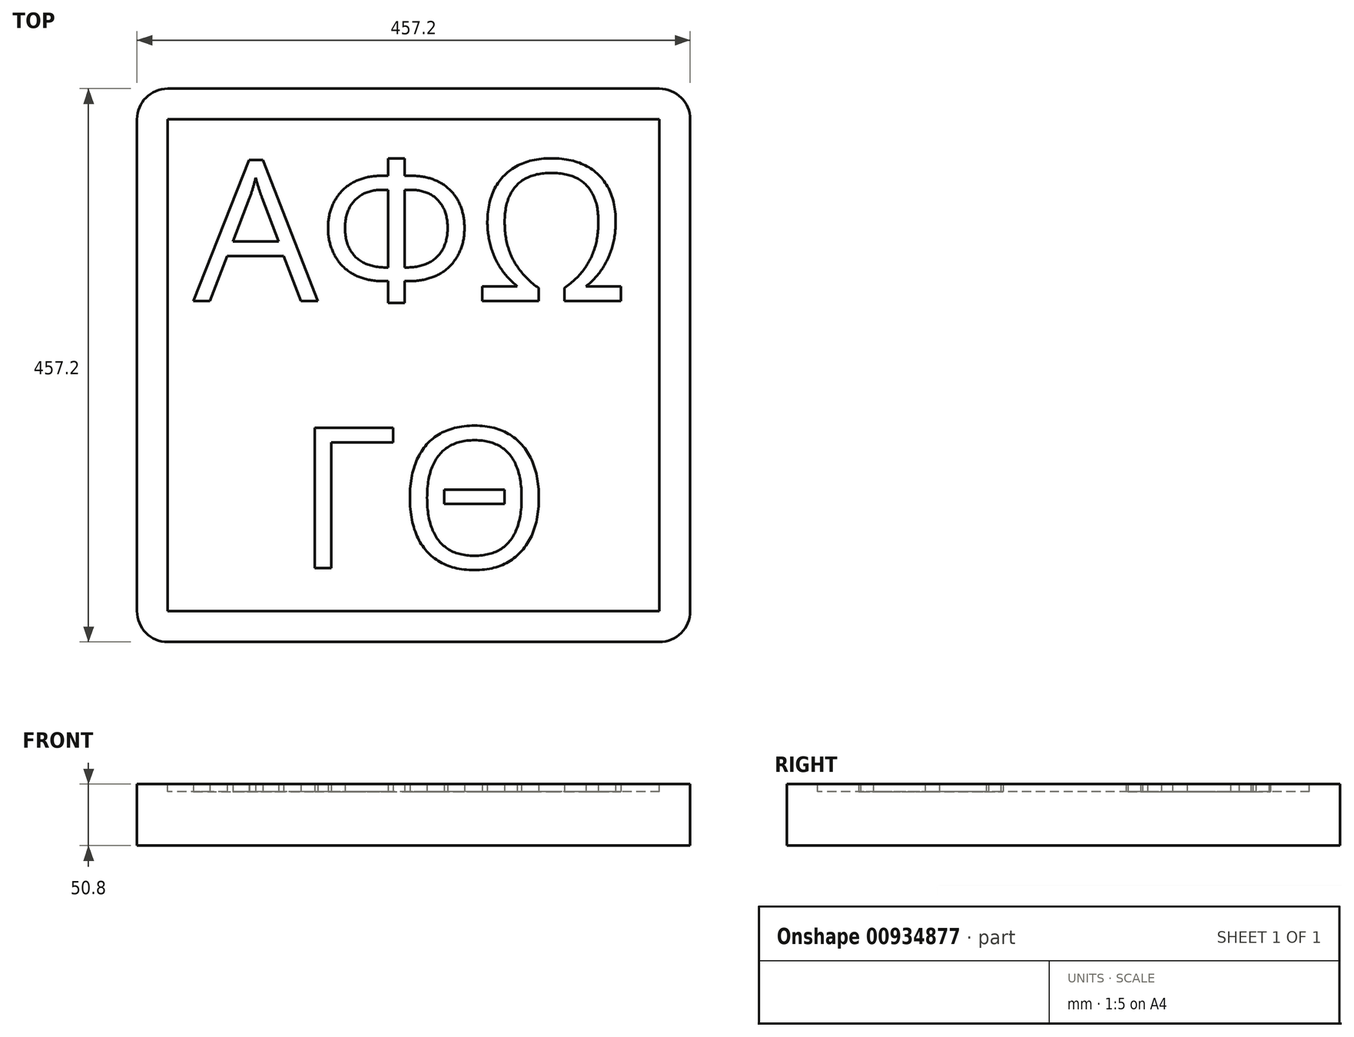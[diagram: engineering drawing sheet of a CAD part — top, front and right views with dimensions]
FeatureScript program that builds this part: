
annotation { "Feature Type Name" : "Feature", "Feature Type Description" : "" }
export const myFeature = defineFeature(function(context is Context, id is Id, definition is map)
    precondition{}
    {
        {
            var Q0;
            Q0=qCreatedBy(makeId("Top.planeOp"),FACE);
            var sketch = newSketch(context, id + "F0", { "sketchPlane" : qUnion([Q0])});
            skLineSegment(sketch, "E0.bottom", {"start": v(228.6, 228.6) * mm, "end": v(-228.6, 228.6) * mm});
            skLineSegment(sketch, "E0.top", {"start": v(228.6, -228.6) * mm, "end": v(-228.6, -228.6) * mm});
            skLineSegment(sketch, "E0.left", {"start": v(228.6, 228.6) * mm, "end": v(228.6, -228.6) * mm});
            skLineSegment(sketch, "E0.right", {"start": v(-228.6, 228.6) * mm, "end": v(-228.6, -228.6) * mm});
            skPoint(sketch, "E0.middle", {"position": v(0, 0) * mm});
            skSolve(sketch);
        }
        {
            var Q0;
            Q0=makeQuery(id+"F0.imprint","IMPRINT",FACE,{"disambiguationData":[TD([[makeQuery(id+"F0.imprint","IMPRINT",EDGE,{"derivedFrom":sQuery(id+"F0.wireOp",EDGE,"E0.bottom")}),1.0]])]});
            extrude(context, id + "F1", {"entities" : qUnion([Q0]), "depth" : 50.8 * mm, "offsetDistance" : 25.4 * mm});
        }
        {
            var Q0;
            Q0=makeQuery(id+"F1.opExtrude","SWEPT_EDGE",EDGE,{"disambiguationData":[OSD([sQuery(id+"F0.wireOp",EDGE,"E0.top"),sQuery(id+"F0.wireOp",EDGE,"E0.right")])]});
            var Q1;
            Q1=makeQuery(id+"F1.opExtrude","SWEPT_EDGE",EDGE,{"disambiguationData":[OSD([sQuery(id+"F0.wireOp",EDGE,"E0.top"),sQuery(id+"F0.wireOp",EDGE,"E0.left")])]});
            var Q2;
            Q2=makeQuery(id+"F1.opExtrude","SWEPT_EDGE",EDGE,{"disambiguationData":[OSD([sQuery(id+"F0.wireOp",EDGE,"E0.bottom"),sQuery(id+"F0.wireOp",EDGE,"E0.left")])]});
            var Q3;
            Q3=makeQuery(id+"F1.opExtrude","SWEPT_EDGE",EDGE,{"disambiguationData":[OSD([sQuery(id+"F0.wireOp",EDGE,"E0.bottom"),sQuery(id+"F0.wireOp",EDGE,"E0.right")])]});
            fillet(context, id + "F2", {"entities" : qUnion([Q0, Q1, Q2, Q3]), "radius" : 25.4 * mm, "tangentPropagation" : true, "allowEdgeOverflow" : false});
        }
        {
            var Q0;
            Q0=makeQuery(id+"F1.opExtrude","CAP_FACE",FACE,{"disambiguationData":[OSD([sQuery(id+"F0.wireOp",EDGE,"E0.bottom"),sQuery(id+"F0.wireOp",EDGE,"E0.top"),sQuery(id+"F0.wireOp",EDGE,"E0.left"),sQuery(id+"F0.wireOp",EDGE,"E0.right")])],"isStart":false});
            var sketch = newSketch(context, id + "F3", { "sketchPlane" : qUnion([Q0])});
            skLineSegment(sketch, "E1.bottom", {"start": v(203.2, 203.2) * mm, "end": v(-203.2, 203.2) * mm});
            skLineSegment(sketch, "E1.top", {"start": v(203.2, -203.2) * mm, "end": v(-203.2, -203.2) * mm});
            skLineSegment(sketch, "E1.left", {"start": v(203.2, 203.2) * mm, "end": v(203.2, -203.2) * mm});
            skLineSegment(sketch, "E1.right", {"start": v(-203.2, 203.2) * mm, "end": v(-203.2, -203.2) * mm});
            skPoint(sketch, "E1.middle", {"position": v(0, 0) * mm});
            skSolve(sketch);
        }
        {
            var Q0;
            Q0=makeQuery(id+"F3.imprint","IMPRINT",FACE,{"disambiguationData":[TD([[makeQuery(id+"F3.imprint","IMPRINT",EDGE,{"derivedFrom":sQuery(id+"F3.wireOp",EDGE,"E1.bottom")}),1.0]])]});
            extrude(context, id + "F4", {"entities" : qUnion([Q0]), "operationType" : NewBodyOperationType.REMOVE, "oppositeDirection" : true, "depth" : 6.35 * mm, "offsetDistance" : 25.4 * mm});
        }
        {
            var Q0;
            Q0=makeQuery(id+"F4.boolean.opBoolean","COPY",FACE,{"derivedFrom":makeQuery(id+"F4.opExtrude","CAP_FACE",FACE,{"disambiguationData":[OSD([sQuery(id+"F3.wireOp",EDGE,"E1.bottom"),sQuery(id+"F3.wireOp",EDGE,"E1.top"),sQuery(id+"F3.wireOp",EDGE,"E1.left"),sQuery(id+"F3.wireOp",EDGE,"E1.right")])],"isStart":false})});
            var sketch = newSketch(context, id + "F5", { "sketchPlane" : qUnion([Q0])});
            skText(sketch, "E2", { "text": "ΑΦΩ\n  ΓΘ", "fontName": "OpenSans-Regular.ttf"});
            skLineSegment(sketch, "E3", {"start": v(-82.05, -170.18) * mm, "end": v(203.2, -170.18) * mm});
            const initialGuessF5  = {"E2": [-0.18186, 0.05325, 1, 0, 0.11693]};
            skSetInitialGuess(sketch, initialGuessF5);
            skSolve(sketch);
        }
        {
            var Q0;
            Q0=makeQuery(id+"F5.imprint","IMPRINT",FACE,{"disambiguationData":[TD([[makeQuery(id+"F5.imprint","IMPRINT",EDGE,{"derivedFrom":sQuery(id+"F5.wireOp",EDGE,"E2.sketch_text.stroke-73")}),-1.0]])]});
            var Q1;
            Q1=makeQuery(id+"F5.imprint","IMPRINT",FACE,{"disambiguationData":[TD([[makeQuery(id+"F5.imprint","IMPRINT",EDGE,{"derivedFrom":sQuery(id+"F5.wireOp",EDGE,"E2.sketch_text.stroke-79")}),-1.0]])]});
            var Q2;
            Q2=makeQuery(id+"F5.imprint","IMPRINT",FACE,{"disambiguationData":[TD([[makeQuery(id+"F5.imprint","IMPRINT",EDGE,{"derivedFrom":sQuery(id+"F5.wireOp",EDGE,"E2.sketch_text.stroke-83")}),-1.0]])]});
            var Q3;
            Q3=makeQuery(id+"F5.imprint","IMPRINT",FACE,{"disambiguationData":[TD([[makeQuery(id+"F5.imprint","IMPRINT",EDGE,{"derivedFrom":sQuery(id+"F5.wireOp",EDGE,"E2.sketch_text.stroke-0")}),-1.0]])]});
            var Q4;
            Q4=makeQuery(id+"F5.imprint","IMPRINT",FACE,{"disambiguationData":[TD([[makeQuery(id+"F5.imprint","IMPRINT",EDGE,{"derivedFrom":sQuery(id+"F5.wireOp",EDGE,"E2.sketch_text.stroke-13")}),-1.0]])]});
            var Q5;
            Q5=makeQuery(id+"F5.imprint","IMPRINT",FACE,{"disambiguationData":[TD([[makeQuery(id+"F5.imprint","IMPRINT",EDGE,{"derivedFrom":sQuery(id+"F5.wireOp",EDGE,"E2.sketch_text.stroke-49")}),-1.0]])]});
            extrude(context, id + "F6", {"entities" : qUnion([Q0, Q1, Q2, Q3, Q4, Q5]), "operationType" : NewBodyOperationType.ADD, "depth" : 6.35 * mm, "offsetDistance" : 25.4 * mm});
        }
    });
